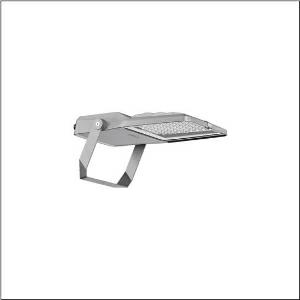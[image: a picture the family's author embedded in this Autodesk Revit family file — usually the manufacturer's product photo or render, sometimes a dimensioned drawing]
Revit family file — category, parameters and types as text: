
# Revit family: floodlight_fl_21_mini___pl43_5xa7773c4a1a_b3c2
name_source: partatom
category: Lighting Fixtures
units: mm (PartAtom-declared; Revit-internal decimal feet)

## family parameters
Cut with Voids When Loaded = No
Host = Face
Light Source = No
Part Type = Normal
Room Calculation Point = No
Round Connector Dimension = Use Diameter
Shared = No

## types (1)
- --- (1 x LED, 20890 lm, 163.5 W, 4000K)
    Apparent Load = 163 VA
    CIE Flux Codes = 27 78 99 100 100
    Color Rendering = 70
    Color Temperature = 4000K
    Default Elevation = 1800 mm
    Description = Floodlight FL 21 mini, floodlight, primary light control with lens, of PMMA, primary optical cover: protective disc, of toughened safety glass, transparent, light distribution: PL43, light emission: direct distribution, installation type: surface-mounted, LED, High Power LED, rated luminous flux: 20.890lm, luminous efficacy: 128lm/W, light colour: 740, colour temperature: 4000K, control gear: ON/OFF Multilumen, control: pre-setting: linear dimming characteristic, Temp-Guard, with terminal, 6-pole, mains connection: 220..240V, AC, 50/60Hz, start of lifetime: 164W, luminaire housing, of diecast aluminium, powder-coated, SITECO metallic grey (DB 702S), corrosivity category C5 mid according to DIN EN ISO 12944, suitable for swimming pools, chlorine-resistant, sealing non-destructively replaceable, mounting bracket, of steel, galvanised, powder-coated, SITECO metallic grey (DB 702S), ON/OFF, protection rating (complete): IP66, insulation class (complete): insulation class I (protective earthing), certification: CE, ENEC, VDE, protection symbol: D, impact resistance: IK08, permissible operating ambient temperature: -40..+40°C, permissible operating ambient temperature for outdoor applications: -40..+50°C, standard: DIN EN 12944, LABS conformity tested according to VDMA 24364:2018-05, packaging unit: 1 piece

Light Distribution: PL43
    Height = 70 mm
    Lamp = 1 x LED
    Lamp Light Flux = 20890 lm
    Lamp Power = 163.5 W
    Lamp count = 1
    Length = 485 mm
    Luminous efficacy = 128 lm/W
    Manufacturer = Siteco
    ModVariant = No
    Model = 5XA7773C4A1A
    Number of Poles = 1
    OnlyDefault = Yes
    Power Factor = 1
    Product Name = Floodlight FL 21 mini | PL43
    Product group = floodlight | pylon annexe
    ProductGroupID = 6201
    Protection Class = Protection class I
    Protection Degree = IP 66
    RLX_Detail_Level = 1
    RLX_Emergency_Light_Flux = 0 lm
    RLX_Emergency_Type = 0
    RLX_Emergency_Type_DB = No
    RlxData = <blob elided: 94289 chars, md5=e4c6fd85>
    Socket = socket
    Standby Power = 0 W
    System Light Flux = 20890 lm
    System Power = 163 W
    Type Comments = factory setting: luminous flux: 100 % | (ON | - | - | - | - | - | - | -) | 825 mA
    Type Image = l_1006845.jpg
    URL = http://relux.com
    VarID = @adj_161161
    Voltage = 0 V
    Weight = 0.00 kg
    Width = 337 mm

## geometry (parser evidence)
native form markers: Blend x4, Sweep x14
no freeform markers — native parametric forms only
